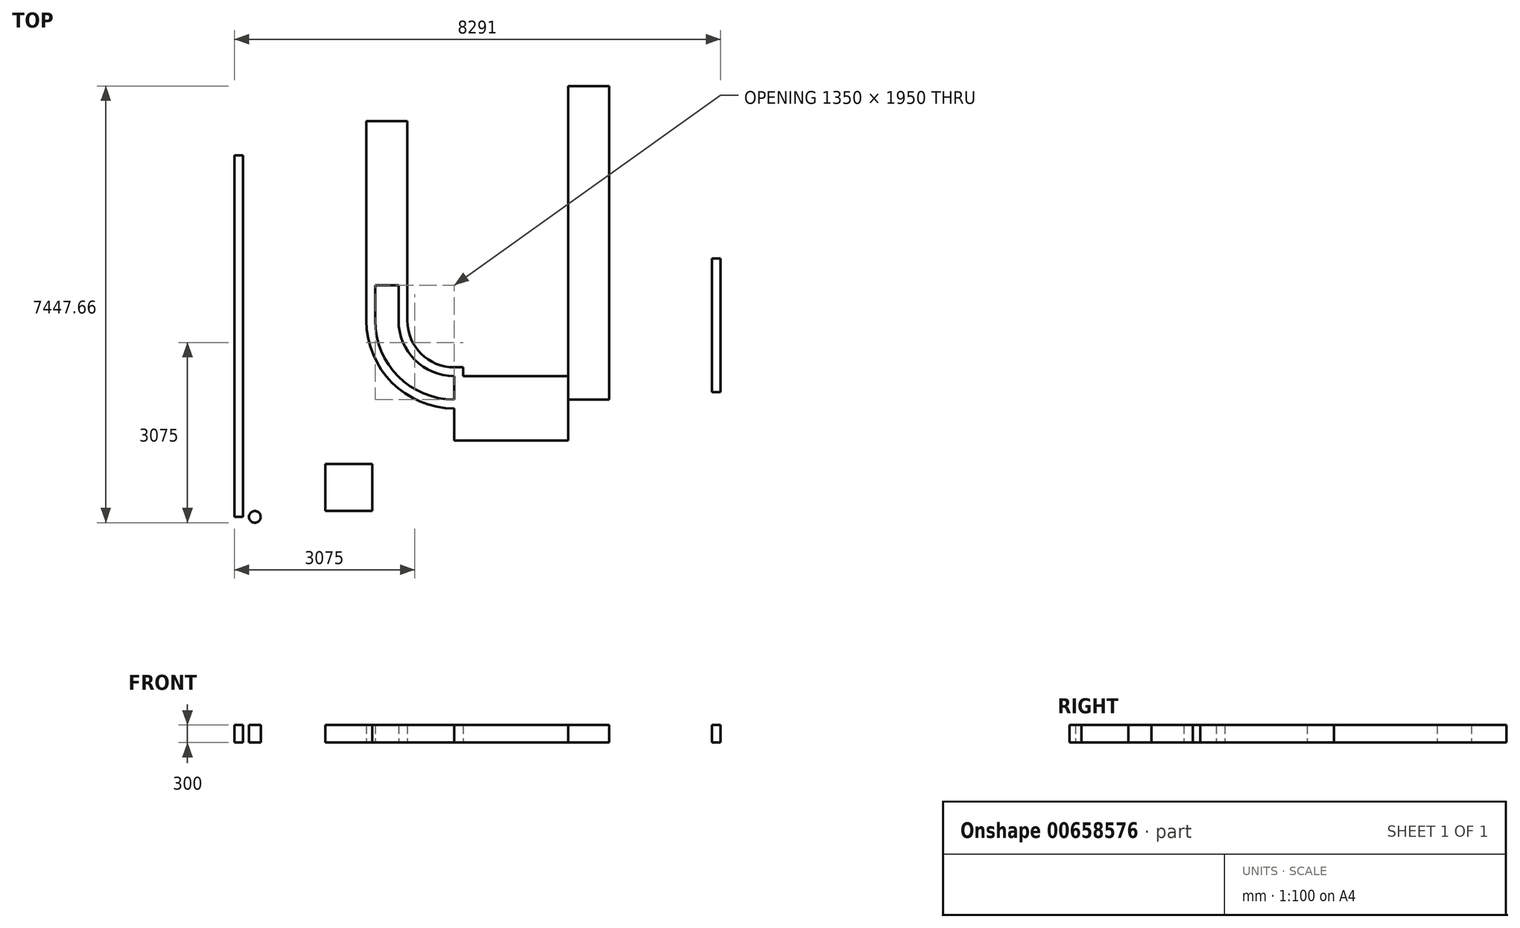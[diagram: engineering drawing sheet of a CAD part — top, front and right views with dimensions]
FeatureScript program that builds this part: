
annotation { "Feature Type Name" : "Feature", "Feature Type Description" : "" }
export const myFeature = defineFeature(function(context is Context, id is Id, definition is map)
    precondition{}
    {
        {
            var Q0;
            Q0=qCreatedBy(makeId("Top.planeOp"),FACE);
            var sketch = newSketch(context, id + "F0", { "sketchPlane" : qUnion([Q0])});
            skLineSegment(sketch, "E0.left", {"start": v(0, 0) * mm, "end": v(0, 3400) * mm});
            skLineSegment(sketch, "E1.bottom", {"start": v(800, -950) * mm, "end": v(2740, -950) * mm});
            skLineSegment(sketch, "E1.top", {"start": v(800, -1350) * mm, "end": v(2740, -1350) * mm});
            skLineSegment(sketch, "E1.left", {"start": v(800, -950) * mm, "end": v(800, -1350) * mm});
            skLineSegment(sketch, "E1.right", {"start": v(2740, -950) * mm, "end": v(2740, -1350) * mm});
            skLineSegment(sketch, "E2", {"start": v(5191, 1057.48) * mm, "end": v(5191, -1222.08) * mm});
            skLineSegment(sketch, "E3.bottom", {"start": v(800, -950) * mm, "end": v(100, -950) * mm, "construction": true});
            skLineSegment(sketch, "E3.top", {"start": v(800, 1450) * mm, "end": v(100, 1450) * mm, "construction": true});
            skLineSegment(sketch, "E3.left", {"start": v(800, -950) * mm, "end": v(800, 1450) * mm, "construction": true});
            skLineSegment(sketch, "E3.right", {"start": v(100, -950) * mm, "end": v(100, 1450) * mm, "construction": true});
            skLineSegment(sketch, "E4", {"start": v(-1400, -3250) * mm, "end": v(-1400, -2450) * mm});
            skLineSegment(sketch, "E5", {"start": v(-1400, -2450) * mm, "end": v(-600, -2450) * mm});
            skLineSegment(sketch, "E6", {"start": v(-600, -2450) * mm, "end": v(-600, -3250) * mm});
            skLineSegment(sketch, "E7", {"start": v(-600, -3250) * mm, "end": v(-1400, -3250) * mm});
            skCircle(sketch, "E8", {"center": v(-2600, -3350) * mm, "radius": 100 * mm});
            skLineSegment(sketch, "E9", {"start": v(5191, 1057.48) * mm, "end": v(5341, 1057.48) * mm});
            skLineSegment(sketch, "E10", {"start": v(5341, 1057.48) * mm, "end": v(5341, -1222.08) * mm});
            skLineSegment(sketch, "E11", {"start": v(5341, -1222.08) * mm, "end": v(5191, -1222.08) * mm});
            skLineSegment(sketch, "E12", {"start": v(100, -950) * mm, "end": v(100, -1350) * mm, "construction": true});
            skLineSegment(sketch, "E13", {"start": v(100, -1350) * mm, "end": v(800, -1350) * mm, "construction": true});
            skLineSegment(sketch, "E14", {"start": v(-2800, -3350) * mm, "end": v(-2800, 2815.93) * mm});
            skLineSegment(sketch, "E15", {"start": v(-2800, 2815.93) * mm, "end": v(-2950, 2815.93) * mm});
            skLineSegment(sketch, "E16", {"start": v(-2950, 2815.93) * mm, "end": v(-2950, -3350) * mm});
            skLineSegment(sketch, "E17", {"start": v(-2950, -3350) * mm, "end": v(-2800, -3350) * mm});
            skLineSegment(sketch, "E18", {"start": v(800, -1350) * mm, "end": v(800, -2050) * mm});
            skLineSegment(sketch, "E19", {"start": v(800, -2050) * mm, "end": v(2740, -2050) * mm});
            skLineSegment(sketch, "E20", {"start": v(2740, -2050) * mm, "end": v(2740, -1350) * mm});
            skLineSegment(sketch, "E21", {"start": v(800, -2050) * mm, "end": v(-600, -2450) * mm, "construction": true});
            skLineSegment(sketch, "E22", {"start": v(800, -1500) * mm, "end": v(2740, -1500) * mm, "construction": true});
            skLineSegment(sketch, "E23", {"start": v(-550, 3400) * mm, "end": v(-550, 0) * mm});
            skLineSegment(sketch, "E24", {"start": v(-150, 3400) * mm, "end": v(-150, 0) * mm});
            skLineSegment(sketch, "E25", {"start": v(-550, 3400) * mm, "end": v(-700, 3400) * mm});
            skLineSegment(sketch, "E26", {"start": v(-700, 3400) * mm, "end": v(-700, 0) * mm});
            skLineSegment(sketch, "E27", {"start": v(800, -800) * mm, "end": v(2740, -800) * mm, "construction": true});
            skArc(sketch, "E28", {"start": v(0, 0) * mm, "mid": v(234.31, -565.69) * mm, "end": v(800, -800) * mm});
            skArc(sketch, "E29", {"start": v(-150, 0) * mm, "mid": v(128.25, -671.75) * mm, "end": v(800, -950) * mm});
            skArc(sketch, "E30", {"start": v(-550, 0) * mm, "mid": v(-154.6, -954.6) * mm, "end": v(800, -1350) * mm});
            skArc(sketch, "E31", {"start": v(-700, 0) * mm, "mid": v(-260.66, -1060.66) * mm, "end": v(800, -1500) * mm});
            skLineSegment(sketch, "E32", {"start": v(-700, 0) * mm, "end": v(-550, 0) * mm});
            skLineSegment(sketch, "E33", {"start": v(-550, 0) * mm, "end": v(-150, 0) * mm});
            skLineSegment(sketch, "E34", {"start": v(-150, 0) * mm, "end": v(0, 0) * mm});
            skLineSegment(sketch, "E35", {"start": v(800, -800) * mm, "end": v(800, -950) * mm});
            skLineSegment(sketch, "E36", {"start": v(-550, 3400) * mm, "end": v(-150, 3400) * mm});
            skLineSegment(sketch, "E37", {"start": v(-150, 3400) * mm, "end": v(0, 3400) * mm});
            skLineSegment(sketch, "E38", {"start": v(800, -800) * mm, "end": v(950, -800) * mm});
            skLineSegment(sketch, "E39", {"start": v(950, -800) * mm, "end": v(950, -950) * mm});
            skLineSegment(sketch, "E40.bottom", {"start": v(2741, -1351) * mm, "end": v(3441, -1351) * mm});
            skLineSegment(sketch, "E40.top", {"start": v(2741, 3997.66) * mm, "end": v(3441, 3997.66) * mm});
            skLineSegment(sketch, "E40.left", {"start": v(2741, -1351) * mm, "end": v(2741, 3997.66) * mm});
            skLineSegment(sketch, "E40.right", {"start": v(3441, -1351) * mm, "end": v(3441, 3997.66) * mm});
            skLineSegment(sketch, "E41", {"start": v(-3684.13, 3307.87) * mm, "end": v(-3684.13, -3761.93) * mm, "construction": true});
            skSolve(sketch);
        }
        {
            var Q0;
            Q0=qSketchRegion(id+"F0",true);
            extrude(context, id + "F1", {"entities" : qUnion([Q0]), "depth" : 300 * mm, "offsetDistance" : 25 * mm});
        }
        {
            var Q0;
            Q0=qCreatedBy(makeId("Top.planeOp"),FACE);
            var sketch = newSketch(context, id + "F2", { "sketchPlane" : qUnion([Q0])});
            skArc(sketch, "E42", {"start": v(-150, 0) * mm, "mid": v(128.25, -671.75) * mm, "end": v(800, -950) * mm});
            skArc(sketch, "E43", {"start": v(-550, 0) * mm, "mid": v(-154.6, -954.6) * mm, "end": v(800, -1350) * mm});
            skLineSegment(sketch, "E44", {"start": v(800, -950) * mm, "end": v(800, -1350) * mm});
            skLineSegment(sketch, "E45", {"start": v(-550, 0) * mm, "end": v(-550, 600) * mm});
            skLineSegment(sketch, "E46", {"start": v(-550, 600) * mm, "end": v(-150, 600) * mm});
            skLineSegment(sketch, "E47", {"start": v(-150, 600) * mm, "end": v(-150, 0) * mm});
            skSolve(sketch);
        }
        {
            var Q0;
            Q0 = qSketchRegion(id + "F2", true);
            extrude(context, id + "F3", {"entities" : qUnion([Q0]), "operationType" : NewBodyOperationType.REMOVE, "depth" : 500 * mm, "offsetDistance" : 25 * mm});
        }
    });
